# Revit family: РДГПК-100
name_source: partatom
category: Арматура трубопроводов
units: mm (PartAtom-declared; Revit-internal decimal feet)

## family parameters
Всегда вертикально = Да
На основе рабочей плоскости = Нет
Общий = Нет
При загрузке вырезать с полостями = Нет
Размер круглого соединителя = Использовать диаметр
Тип детали = Клапан - Вставляется

## types (12) — shared parameters
ADSK_Единица измерения = шт.
ADSK_Завод-изготовитель = РУП "БЕЛГАЗТЕХНИКА"
ADSK_Количество = 1
ADSK_Марка = РДГПК-100
ADSK_Тип соединения = фланцевое
zero-valued in all types: Отметка по умолчанию

## per-type parameters (varying)
| type | ADSK_Диапазон выходного давления, МПа | ADSK_Наименование | исполнение 100 | исполнение 100-1 |
| РДГПК-100 0,0012-0,0022 | 0,0012 – 0,0022 | Регулятор РДГПК-100;0,0012-0,0022 МПа ТУ РБ 05550283.047-97 | Да | Нет |
| РДГПК-100 0,0015-0,0025 | 0,0015-0,0025 | Регулятор РДГПК-100;0,0015-0,0025 МПа ТУ РБ 05550283.047-97 | Да | Нет |
| РДГПК-100 0,0020-0,0035 | 0,0020-0,0035 | Регулятор РДГПК-100;0,0020-0,0035 МПа ТУ РБ 05550283.047-97 | Да | Нет |
| РДГПК-100 0,0030-0,0045 | 0,0030-0,0045 | Регулятор РДГПК-100;0,0030-0,0045 МПа ТУ РБ 05550283.047-97 | Да | Нет |
| РДГПК-100 0,0040-0,0090 | 0,0040-0,0090 | Регулятор РДГПК-100;0,0040-0,0090 МПа ТУ РБ 05550283.047-97 | Да | Нет |
| РДГПК-100 0,0080-0,0160 | 0,0080-0,0160 | Регулятор РДГПК-100;0,0080-0,0160 МПа ТУ РБ 05550283.047-97 | Да | Нет |
| РДГПК-100-1 0,0012-0,0022 | 0,0012 – 0,0022 | Регулятор РДГПК-100-1;0,0012-0,0022 МПа ТУ РБ 05550283.047-97 | Нет | Да |
| РДГПК-100-1 0,0015-0,0025 | 0,0015-0,0025 | Регулятор РДГПК-100-1;0,0015-0,0025 МПа ТУ РБ 05550283.047-97 | Нет | Да |
| РДГПК-100-1 0,0020-0,0035 | 0,0020-0,0035 | Регулятор РДГПК-100-1;0,0020-0,0035 МПа ТУ РБ 05550283.047-97 | Нет | Да |
| РДГПК-100-1 0,0030-0,0045 | 0,0030-0,0045 | Регулятор РДГПК-100-1;0,0030-0,0045 МПа ТУ РБ 05550283.047-97 | Нет | Да |
| РДГПК-100-1 0,0040-0,0090 | 0,0040-0,0090 | Регулятор РДГПК-100-1;0,0040-0,0090 МПа ТУ РБ 05550283.047-97 | Нет | Да |
| РДГПК-100-1 0,0080-0,0160 | 0,0080-0,0160 | Регулятор РДГПК-100-1;0,0080-0,0160 МПа ТУ РБ 05550283.047-97 | Нет | Да |
